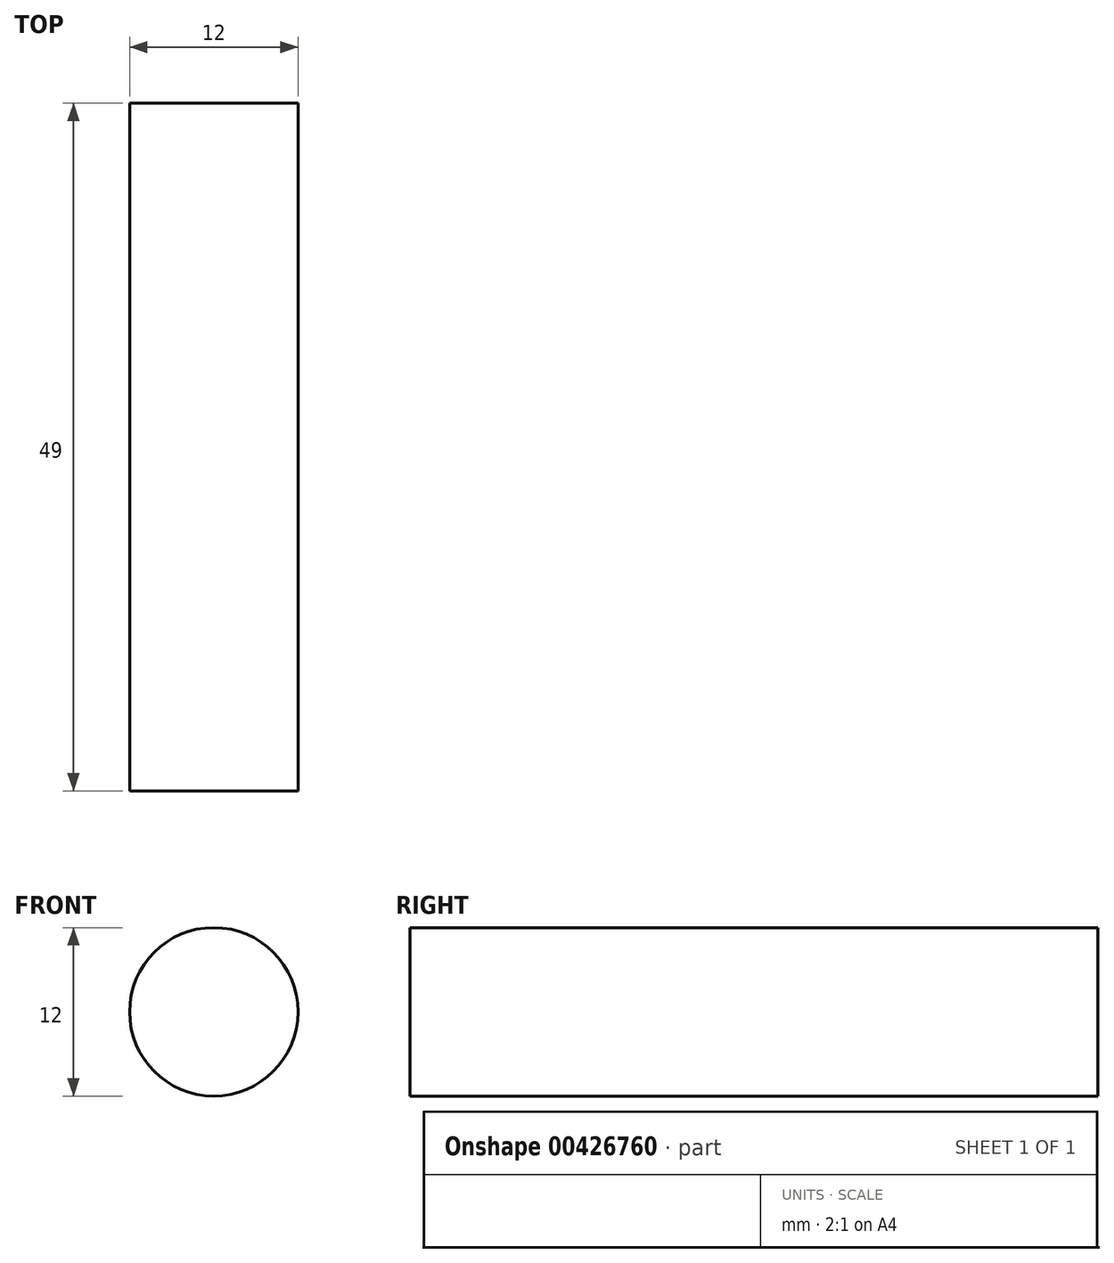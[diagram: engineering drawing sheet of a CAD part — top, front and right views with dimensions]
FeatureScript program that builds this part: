
annotation { "Feature Type Name" : "Feature", "Feature Type Description" : "" }
export const myFeature = defineFeature(function(context is Context, id is Id, definition is map)
    precondition{}
    {
        {
            var Q0;
            Q0=qCreatedBy(makeId("Front.planeOp"),FACE);
            var sketch = newSketch(context, id + "F0", { "sketchPlane" : qUnion([Q0])});
            skCircle(sketch, "E0", {"center": v(0, 0) * mm, "radius": 6 * mm});
            skSolve(sketch);
        }
        {
            var Q0;
            Q0=makeQuery(id+"F0.imprint","IMPRINT",FACE,{"disambiguationData":[TD([[makeQuery(id+"F0.imprint","IMPRINT",EDGE,{"derivedFrom":sQuery(id+"F0.wireOp",EDGE,"E0")}),1.0]])]});
            extrude(context, id + "F1", {"entities" : qUnion([Q0]), "depth" : 49 * mm});
        }
    });
